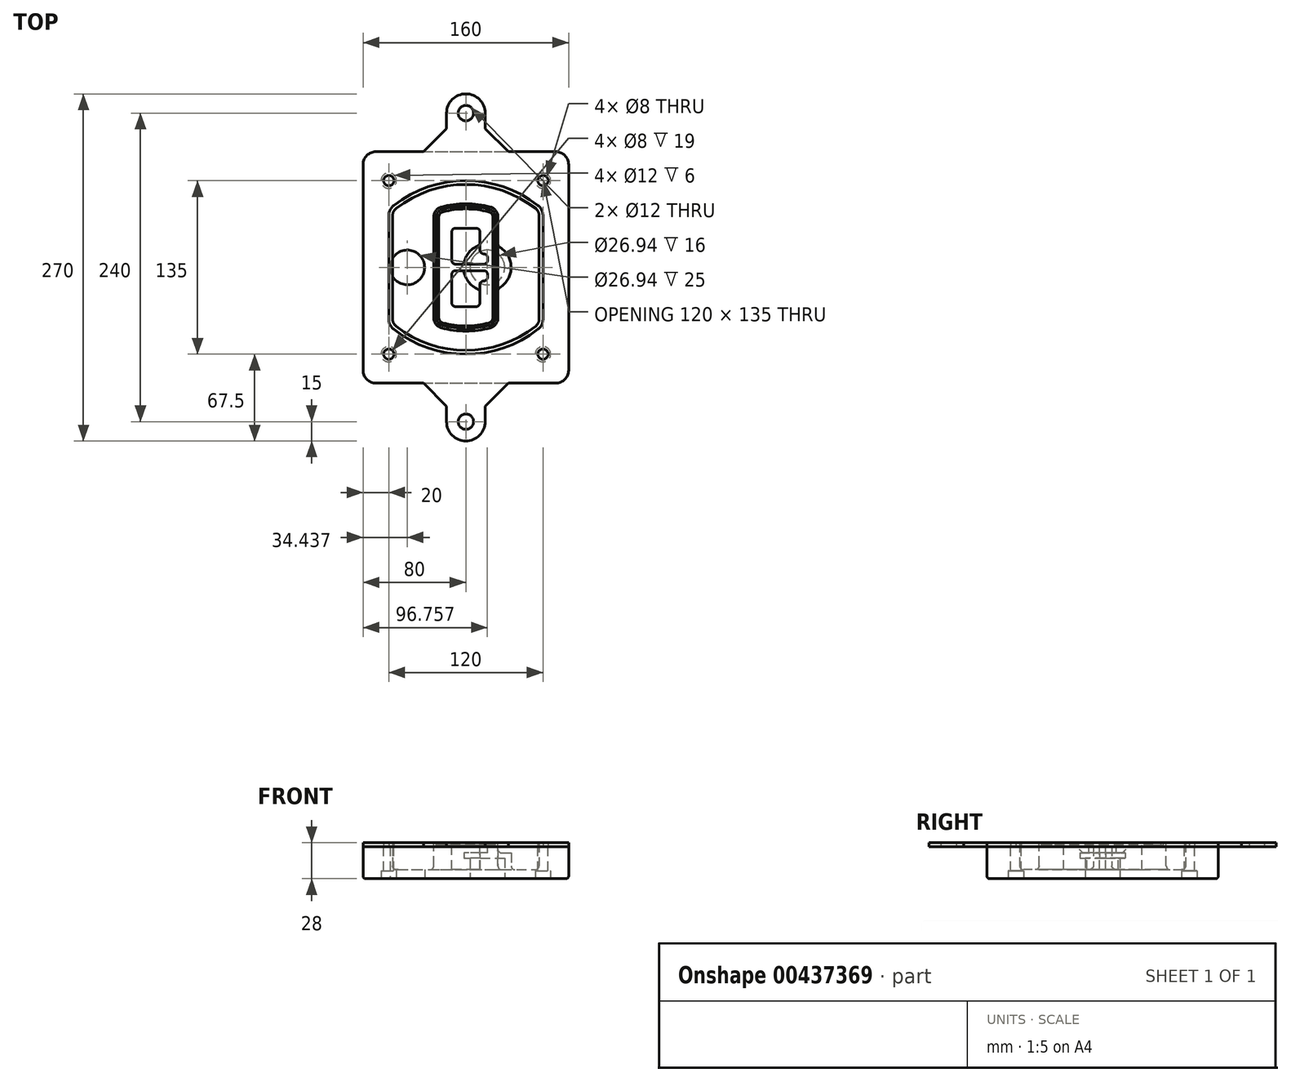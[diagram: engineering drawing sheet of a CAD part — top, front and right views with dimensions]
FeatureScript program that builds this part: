
annotation { "Feature Type Name" : "Feature", "Feature Type Description" : "" }
export const myFeature = defineFeature(function(context is Context, id is Id, definition is map)
    precondition{}
    {
        {
            var Q0;
            Q0=qCreatedBy(makeId("Top.planeOp"),FACE);
            var sketch = newSketch(context, id + "F0", { "sketchPlane" : qUnion([Q0])});
            skPoint(sketch, "E0.rect.middle", {"position": v(0, 0) * mm});
            skLineSegment(sketch, "E1.bottom", {"start": v(-70, -90) * mm, "end": v(70, -90) * mm});
            skLineSegment(sketch, "E1.top", {"start": v(-70, 90) * mm, "end": v(70, 90) * mm});
            skLineSegment(sketch, "E1.left", {"start": v(-80, -80) * mm, "end": v(-80, 80) * mm});
            skLineSegment(sketch, "E1.right", {"start": v(80, -80) * mm, "end": v(80, 80) * mm});
            skLineSegment(sketch, "E2", {"start": v(-80, 90) * mm, "end": v(80, -90) * mm, "construction": true});
            skLineSegment(sketch, "E3", {"start": v(80, 90) * mm, "end": v(-80, -90) * mm, "construction": true});
            skCircle(sketch, "E4", {"center": v(-60, 67.5) * mm, "radius": 4 * mm});
            skCircle(sketch, "E5", {"center": v(60, 67.5) * mm, "radius": 4 * mm});
            skCircle(sketch, "E6", {"center": v(60, -67.5) * mm, "radius": 4 * mm});
            skCircle(sketch, "E7", {"center": v(-60, -67.5) * mm, "radius": 4 * mm});
            skLineSegment(sketch, "E8", {"start": v(-60, 67.5) * mm, "end": v(60, 67.5) * mm, "construction": true});
            skLineSegment(sketch, "E9", {"start": v(60, 67.5) * mm, "end": v(60, -67.5) * mm, "construction": true});
            skLineSegment(sketch, "E10", {"start": v(60, -67.5) * mm, "end": v(-60, -67.5) * mm, "construction": true});
            skLineSegment(sketch, "E11", {"start": v(-60, -67.5) * mm, "end": v(-60, 67.5) * mm, "construction": true});
            skLineSegment(sketch, "E12", {"start": v(-60, 40.3) * mm, "end": v(-60, -40.3) * mm});
            skLineSegment(sketch, "E13", {"start": v(60, 40.3) * mm, "end": v(60, -40.3) * mm});
            skArc(sketch, "E14", {"start": v(56.15, 48.18) * mm, "mid": v(0, 67.5) * mm, "end": v(-56.15, 48.18) * mm});
            skArc(sketch, "E15", {"start": v(-56.15, -48.18) * mm, "mid": v(0, -67.5) * mm, "end": v(56.15, -48.18) * mm});
            skLineSegment(sketch, "E16", {"start": v(-60, 0) * mm, "end": v(60, 0) * mm, "construction": true});
            skPoint(sketch, "E17.visualSharp", {"position": v(-60, -45) * mm});
            skArc(sketch, "E17.filletArc", {"start": v(-60, -40.3) * mm, "mid": v(-58.99, -44.68) * mm, "end": v(-56.15, -48.18) * mm});
            skPoint(sketch, "E18.visualSharp", {"position": v(-60, 45) * mm});
            skArc(sketch, "E18.filletArc", {"start": v(-56.15, 48.18) * mm, "mid": v(-58.99, 44.68) * mm, "end": v(-60, 40.3) * mm});
            skPoint(sketch, "E19.visualSharp", {"position": v(60, 45) * mm});
            skArc(sketch, "E19.filletArc", {"start": v(60, 40.3) * mm, "mid": v(58.99, 44.68) * mm, "end": v(56.15, 48.18) * mm});
            skPoint(sketch, "E20.visualSharp", {"position": v(60, -45) * mm});
            skArc(sketch, "E20.filletArc", {"start": v(56.15, -48.18) * mm, "mid": v(58.99, -44.68) * mm, "end": v(60, -40.3) * mm});
            skPoint(sketch, "E21.visualSharp", {"position": v(-80, 90) * mm});
            skArc(sketch, "E21.filletArc", {"start": v(-70, 90) * mm, "mid": v(-77.07, 87.07) * mm, "end": v(-80, 80) * mm});
            skPoint(sketch, "E22.visualSharp", {"position": v(80, 90) * mm});
            skArc(sketch, "E22.filletArc", {"start": v(80, 80) * mm, "mid": v(77.07, 87.07) * mm, "end": v(70, 90) * mm});
            skPoint(sketch, "E23.visualSharp", {"position": v(80, -90) * mm});
            skArc(sketch, "E23.filletArc", {"start": v(70, -90) * mm, "mid": v(77.07, -87.07) * mm, "end": v(80, -80) * mm});
            skPoint(sketch, "E24.visualSharp", {"position": v(-80, -90) * mm});
            skArc(sketch, "E24.filletArc", {"start": v(-80, -80) * mm, "mid": v(-77.07, -87.07) * mm, "end": v(-70, -90) * mm});
            skArc(sketch, "E25.0", {"start": v(57, 40.3) * mm, "mid": v(56.3, 43.36) * mm, "end": v(54.3, 45.81) * mm});
            skLineSegment(sketch, "E25.1", {"start": v(57, 40.3) * mm, "end": v(57, -40.3) * mm});
            skArc(sketch, "E25.2", {"start": v(54.3, -45.81) * mm, "mid": v(56.3, -43.36) * mm, "end": v(57, -40.3) * mm});
            skArc(sketch, "E25.3", {"start": v(-54.3, -45.81) * mm, "mid": v(0, -64.5) * mm, "end": v(54.3, -45.81) * mm});
            skArc(sketch, "E25.4", {"start": v(-57, -40.3) * mm, "mid": v(-56.3, -43.36) * mm, "end": v(-54.3, -45.81) * mm});
            skArc(sketch, "E25.5", {"start": v(54.3, 45.81) * mm, "mid": v(0, 64.5) * mm, "end": v(-54.3, 45.81) * mm});
            skLineSegment(sketch, "E25.6", {"start": v(-57, 40.3) * mm, "end": v(-57, -40.3) * mm});
            skArc(sketch, "E25.7", {"start": v(-54.3, 45.81) * mm, "mid": v(-56.3, 43.36) * mm, "end": v(-57, 40.3) * mm});
            skArc(sketch, "E26.0", {"start": v(-58.62, 51.33) * mm, "mid": v(-62.58, 46.43) * mm, "end": v(-64, 40.3) * mm});
            skArc(sketch, "E26.1", {"start": v(58.62, 51.33) * mm, "mid": v(0, 71.5) * mm, "end": v(-58.62, 51.33) * mm});
            skArc(sketch, "E26.2", {"start": v(64, 40.3) * mm, "mid": v(62.58, 46.43) * mm, "end": v(58.62, 51.33) * mm});
            skLineSegment(sketch, "E26.3", {"start": v(64, 40.3) * mm, "end": v(64, -40.3) * mm});
            skArc(sketch, "E26.4", {"start": v(58.62, -51.33) * mm, "mid": v(62.58, -46.43) * mm, "end": v(64, -40.3) * mm});
            skLineSegment(sketch, "E26.5", {"start": v(-64, 40.3) * mm, "end": v(-64, -40.3) * mm});
            skArc(sketch, "E26.6", {"start": v(-58.62, -51.33) * mm, "mid": v(0, -71.5) * mm, "end": v(58.62, -51.33) * mm});
            skArc(sketch, "E26.7", {"start": v(-64, -40.3) * mm, "mid": v(-62.58, -46.43) * mm, "end": v(-58.62, -51.33) * mm});
            skSolve(sketch);
        }
        {
            var Q0;
            Q0=makeQuery(id+"F0.imprint","IMPRINT",FACE,{"disambiguationData":[TD([[makeQuery(id+"F0.imprint","IMPRINT",EDGE,{"derivedFrom":sQuery(id+"F0.wireOp",EDGE,"E1.bottom")}),1.0]])]});
            var Q1;
            Q1=makeQuery(id+"F0.imprint","IMPRINT",FACE,{"disambiguationData":[TD([[makeQuery(id+"F0.imprint","IMPRINT",EDGE,{"derivedFrom":sQuery(id+"F0.wireOp",EDGE,"E12")}),1.0]])]});
            var Q2;
            Q2=makeQuery(id+"F0.imprint","IMPRINT",FACE,{"disambiguationData":[TD([[makeQuery(id+"F0.imprint","IMPRINT",EDGE,{"derivedFrom":sQuery(id+"F0.wireOp",EDGE,"E25.0")}),1.0]])]});
            var Q3;
            Q3=makeQuery(id+"F0.imprint","IMPRINT",FACE,{"disambiguationData":[TD([[makeQuery(id+"F0.imprint","IMPRINT",EDGE,{"derivedFrom":sQuery(id+"F0.wireOp",EDGE,"E12")}),-1.0]])]});
            extrude(context, id + "F1", {"entities" : qUnion([Q0, Q1, Q2, Q3]), "oppositeDirection" : true, "depth" : 25 * mm});
        }
        {
            var Q0;
            Q0=makeQuery(id+"F0.imprint","IMPRINT",FACE,{"disambiguationData":[TD([[makeQuery(id+"F0.imprint","IMPRINT",EDGE,{"derivedFrom":sQuery(id+"F0.wireOp",EDGE,"E12")}),1.0]])]});
            extrude(context, id + "F2", {"entities" : qUnion([Q0]), "operationType" : NewBodyOperationType.ADD, "depth" : 3 * mm});
        }
        {
            var Q0;
            Q0=makeQuery(id+"F0.imprint","IMPRINT",FACE,{"disambiguationData":[TD([[makeQuery(id+"F0.imprint","IMPRINT",EDGE,{"derivedFrom":sQuery(id+"F0.wireOp",EDGE,"E25.0")}),1.0]])]});
            extrude(context, id + "F3", {"entities" : qUnion([Q0]), "operationType" : NewBodyOperationType.REMOVE, "oppositeDirection" : true, "depth" : 18 * mm});
        }
        {
            var Q0;
            Q0=makeQuery(id+"F2.opExtrude","CAP_FACE",FACE,{"disambiguationData":[OSD([sQuery(id+"F0.wireOp",EDGE,"E12"),sQuery(id+"F0.wireOp",EDGE,"E13"),sQuery(id+"F0.wireOp",EDGE,"E14"),sQuery(id+"F0.wireOp",EDGE,"E15"),sQuery(id+"F0.wireOp",EDGE,"E17.filletArc"),sQuery(id+"F0.wireOp",EDGE,"E18.filletArc"),sQuery(id+"F0.wireOp",EDGE,"E19.filletArc"),sQuery(id+"F0.wireOp",EDGE,"E20.filletArc"),sQuery(id+"F0.wireOp",EDGE,"E25.0"),sQuery(id+"F0.wireOp",EDGE,"E25.1"),sQuery(id+"F0.wireOp",EDGE,"E25.2"),sQuery(id+"F0.wireOp",EDGE,"E25.3"),sQuery(id+"F0.wireOp",EDGE,"E25.4"),sQuery(id+"F0.wireOp",EDGE,"E25.5"),sQuery(id+"F0.wireOp",EDGE,"E25.6"),sQuery(id+"F0.wireOp",EDGE,"E25.7")])],"isStart":false});
            var sketch = newSketch(context, id + "F4", { "sketchPlane" : qUnion([Q0])});
            skArc(sketch, "E27.0", {"start": v(-19.08, -46.97) * mm, "mid": v(0, -49.5) * mm, "end": v(19.08, -46.97) * mm});
            skArc(sketch, "E28.0", {"start": v(19.08, 46.97) * mm, "mid": v(0, 49.5) * mm, "end": v(-19.08, 46.97) * mm});
            skLineSegment(sketch, "E29", {"start": v(-25, 39.25) * mm, "end": v(-25, -39.25) * mm});
            skLineSegment(sketch, "E30", {"start": v(25, 39.25) * mm, "end": v(25, -39.25) * mm});
            skLineSegment(sketch, "E31", {"start": v(-25, 45.1) * mm, "end": v(25, 45.1) * mm, "construction": true});
            skLineSegment(sketch, "E32", {"start": v(-25, -45.1) * mm, "end": v(25, -45.1) * mm, "construction": true});
            skPoint(sketch, "E33.visualSharp", {"position": v(-25, 45.1) * mm});
            skArc(sketch, "E33.filletArc", {"start": v(-19.08, 46.97) * mm, "mid": v(-23.35, 44.11) * mm, "end": v(-25, 39.25) * mm});
            skPoint(sketch, "E34.visualSharp", {"position": v(25, 45.1) * mm});
            skArc(sketch, "E34.filletArc", {"start": v(25, 39.25) * mm, "mid": v(23.35, 44.11) * mm, "end": v(19.08, 46.97) * mm});
            skPoint(sketch, "E35.visualSharp", {"position": v(25, -45.1) * mm});
            skArc(sketch, "E35.filletArc", {"start": v(19.08, -46.97) * mm, "mid": v(23.35, -44.11) * mm, "end": v(25, -39.25) * mm});
            skPoint(sketch, "E36.visualSharp", {"position": v(-25, -45.1) * mm});
            skArc(sketch, "E36.filletArc", {"start": v(-25, -39.25) * mm, "mid": v(-23.35, -44.11) * mm, "end": v(-19.08, -46.97) * mm});
            skArc(sketch, "E37.0", {"start": v(54.3, 45.81) * mm, "mid": v(0, 64.5) * mm, "end": v(-54.3, 45.81) * mm});
            skArc(sketch, "E37.1", {"start": v(-54.3, 45.81) * mm, "mid": v(-56.3, 43.36) * mm, "end": v(-57, 40.3) * mm});
            skLineSegment(sketch, "E37.2", {"start": v(-57, 40.3) * mm, "end": v(-57, -40.3) * mm});
            skArc(sketch, "E37.3", {"start": v(-57, -40.3) * mm, "mid": v(-56.3, -43.36) * mm, "end": v(-54.3, -45.81) * mm});
            skArc(sketch, "E37.4", {"start": v(-54.3, -45.81) * mm, "mid": v(0, -64.5) * mm, "end": v(54.3, -45.81) * mm});
            skArc(sketch, "E37.5", {"start": v(54.3, -45.81) * mm, "mid": v(56.3, -43.36) * mm, "end": v(57, -40.3) * mm});
            skLineSegment(sketch, "E37.6", {"start": v(57, 40.3) * mm, "end": v(57, -40.3) * mm});
            skArc(sketch, "E37.7", {"start": v(57, 40.3) * mm, "mid": v(56.3, 43.36) * mm, "end": v(54.3, 45.81) * mm});
            skLineSegment(sketch, "E38.0", {"start": v(23, 39.25) * mm, "end": v(23, -39.25) * mm});
            skArc(sketch, "E38.1", {"start": v(18.56, -45.04) * mm, "mid": v(21.76, -42.9) * mm, "end": v(23, -39.25) * mm});
            skArc(sketch, "E38.2", {"start": v(-18.56, -45.04) * mm, "mid": v(0, -47.5) * mm, "end": v(18.56, -45.04) * mm});
            skArc(sketch, "E38.3", {"start": v(-23, -39.25) * mm, "mid": v(-21.76, -42.9) * mm, "end": v(-18.56, -45.04) * mm});
            skLineSegment(sketch, "E38.4", {"start": v(-23, 39.25) * mm, "end": v(-23, -39.25) * mm});
            skArc(sketch, "E38.5", {"start": v(23, 39.25) * mm, "mid": v(21.76, 42.9) * mm, "end": v(18.56, 45.04) * mm});
            skArc(sketch, "E38.6", {"start": v(-18.56, 45.04) * mm, "mid": v(-21.76, 42.9) * mm, "end": v(-23, 39.25) * mm});
            skArc(sketch, "E38.7", {"start": v(18.56, 45.04) * mm, "mid": v(0, 47.5) * mm, "end": v(-18.56, 45.04) * mm});
            skArc(sketch, "E39.0", {"start": v(21, 39.25) * mm, "mid": v(20.18, 41.68) * mm, "end": v(18.04, 43.1) * mm});
            skLineSegment(sketch, "E39.1", {"start": v(21, 39.25) * mm, "end": v(21, -39.25) * mm});
            skArc(sketch, "E39.2", {"start": v(18.04, -43.1) * mm, "mid": v(20.18, -41.68) * mm, "end": v(21, -39.25) * mm});
            skArc(sketch, "E39.3", {"start": v(-18.04, -43.1) * mm, "mid": v(0, -45.5) * mm, "end": v(18.04, -43.1) * mm});
            skArc(sketch, "E39.4", {"start": v(-21, -39.25) * mm, "mid": v(-20.18, -41.68) * mm, "end": v(-18.04, -43.1) * mm});
            skArc(sketch, "E39.5", {"start": v(18.04, 43.1) * mm, "mid": v(0, 45.5) * mm, "end": v(-18.04, 43.1) * mm});
            skLineSegment(sketch, "E39.6", {"start": v(-21, 39.25) * mm, "end": v(-21, -39.25) * mm});
            skArc(sketch, "E39.7", {"start": v(-18.04, 43.1) * mm, "mid": v(-20.18, 41.68) * mm, "end": v(-21, 39.25) * mm});
            skLineSegment(sketch, "E40", {"start": v(-25, 0) * mm, "end": v(25, 0) * mm, "construction": true});
            skLineSegment(sketch, "E41", {"start": v(-11, 5.5) * mm, "end": v(-11, 27.5) * mm});
            skLineSegment(sketch, "E42", {"start": v(-8, 30.5) * mm, "end": v(8, 30.5) * mm});
            skLineSegment(sketch, "E43", {"start": v(11, 27.5) * mm, "end": v(11, 13.5) * mm});
            skLineSegment(sketch, "E44", {"start": v(14, 10.5) * mm, "end": v(14, 10.5) * mm});
            skLineSegment(sketch, "E45", {"start": v(17, 7.5) * mm, "end": v(17, 5.5) * mm});
            skLineSegment(sketch, "E46", {"start": v(14, 2.5) * mm, "end": v(-8, 2.5) * mm});
            skPoint(sketch, "E47.visualSharp", {"position": v(-11, 30.5) * mm});
            skArc(sketch, "E47.filletArc", {"start": v(-8, 30.5) * mm, "mid": v(-10.12, 29.62) * mm, "end": v(-11, 27.5) * mm});
            skPoint(sketch, "E48.visualSharp", {"position": v(11, 30.5) * mm});
            skArc(sketch, "E48.filletArc", {"start": v(11, 27.5) * mm, "mid": v(10.12, 29.62) * mm, "end": v(8, 30.5) * mm});
            skPoint(sketch, "E49.visualSharp", {"position": v(11, 10.5) * mm});
            skArc(sketch, "E49.filletArc", {"start": v(11, 13.5) * mm, "mid": v(11.88, 11.38) * mm, "end": v(14, 10.5) * mm});
            skPoint(sketch, "E50.visualSharp", {"position": v(17, 10.5) * mm});
            skArc(sketch, "E50.filletArc", {"start": v(17, 7.5) * mm, "mid": v(16.12, 9.62) * mm, "end": v(14, 10.5) * mm});
            skPoint(sketch, "E51.visualSharp", {"position": v(17, 2.5) * mm});
            skArc(sketch, "E51.filletArc", {"start": v(14, 2.5) * mm, "mid": v(16.12, 3.38) * mm, "end": v(17, 5.5) * mm});
            skPoint(sketch, "E52.visualSharp", {"position": v(-11, 2.5) * mm});
            skArc(sketch, "E52.filletArc", {"start": v(-11, 5.5) * mm, "mid": v(-10.12, 3.38) * mm, "end": v(-8, 2.5) * mm});
            skLineSegment(sketch, "E53.0.MirrorCS", {"start": v(14, -2.5) * mm, "end": v(-8, -2.5) * mm});
            skArc(sketch, "E54.0.MirrorCS", {"start": v(-11, -5.5) * mm, "mid": v(-10.12, -3.38) * mm, "end": v(-8, -2.5) * mm});
            skLineSegment(sketch, "E55.0.MirrorCS", {"start": v(-11, -5.5) * mm, "end": v(-11, -27.5) * mm});
            skArc(sketch, "E56.0.MirrorCS", {"start": v(-8, -30.5) * mm, "mid": v(-10.12, -29.62) * mm, "end": v(-11, -27.5) * mm});
            skLineSegment(sketch, "E57.0.MirrorCS", {"start": v(-8, -30.5) * mm, "end": v(8, -30.5) * mm});
            skArc(sketch, "E58.0.MirrorCS", {"start": v(11, -27.5) * mm, "mid": v(10.12, -29.62) * mm, "end": v(8, -30.5) * mm});
            skLineSegment(sketch, "E59.0.MirrorCS", {"start": v(11, -27.5) * mm, "end": v(11, -13.5) * mm});
            skArc(sketch, "E60.0.MirrorCS", {"start": v(11, -13.5) * mm, "mid": v(11.88, -11.38) * mm, "end": v(14, -10.5) * mm});
            skArc(sketch, "E61.0.MirrorCS", {"start": v(17, -7.5) * mm, "mid": v(16.12, -9.62) * mm, "end": v(14, -10.5) * mm});
            skLineSegment(sketch, "E62.0.MirrorCS", {"start": v(17, -7.5) * mm, "end": v(17, -5.5) * mm});
            skArc(sketch, "E63.0.MirrorCS", {"start": v(14, -2.5) * mm, "mid": v(16.12, -3.38) * mm, "end": v(17, -5.5) * mm});
            skSolve(sketch);
        }
        {
            var Q0;
            Q0=makeQuery(id+"F4.imprint","IMPRINT",FACE,{"disambiguationData":[TD([[makeQuery(id+"F4.imprint","IMPRINT",EDGE,{"derivedFrom":sQuery(id+"F4.wireOp",EDGE,"E27.0")}),1.0]])]});
            var Q1;
            Q1=makeQuery(id+"F4.imprint","IMPRINT",FACE,{"disambiguationData":[TD([[makeQuery(id+"F4.imprint","IMPRINT",EDGE,{"derivedFrom":sQuery(id+"F4.wireOp",EDGE,"E38.0")}),-1.0]])]});
            var Q2;
            Q2=makeQuery(id+"F4.imprint","IMPRINT",FACE,{"disambiguationData":[TD([[makeQuery(id+"F4.imprint","IMPRINT",EDGE,{"derivedFrom":sQuery(id+"F4.wireOp",EDGE,"E39.0")}),1.0]])]});
            extrude(context, id + "F5", {"entities" : qUnion([Q0, Q1, Q2]), "operationType" : NewBodyOperationType.ADD, "endBound" : BoundingType.UP_TO_NEXT, "oppositeDirection" : true, "depth" : 25 * mm});
        }
        {
            var Q0;
            Q0=makeQuery(id+"F4.imprint","IMPRINT",FACE,{"disambiguationData":[TD([[makeQuery(id+"F4.imprint","IMPRINT",EDGE,{"derivedFrom":sQuery(id+"F4.wireOp",EDGE,"E38.0")}),-1.0]])]});
            extrude(context, id + "F6", {"entities" : qUnion([Q0]), "operationType" : NewBodyOperationType.REMOVE, "oppositeDirection" : true, "depth" : 2 * mm});
        }
        {
            var Q0;
            Q0=makeQuery(id+"F1.opExtrude","CAP_FACE",FACE,{"disambiguationData":[OSD([sQuery(id+"F0.wireOp",EDGE,"E1.bottom"),sQuery(id+"F0.wireOp",EDGE,"E1.top"),sQuery(id+"F0.wireOp",EDGE,"E1.left"),sQuery(id+"F0.wireOp",EDGE,"E1.right"),sQuery(id+"F0.wireOp",EDGE,"E4"),sQuery(id+"F0.wireOp",EDGE,"E5"),sQuery(id+"F0.wireOp",EDGE,"E6"),sQuery(id+"F0.wireOp",EDGE,"E7"),sQuery(id+"F0.wireOp",EDGE,"E21.filletArc"),sQuery(id+"F0.wireOp",EDGE,"E22.filletArc"),sQuery(id+"F0.wireOp",EDGE,"E23.filletArc"),sQuery(id+"F0.wireOp",EDGE,"E24.filletArc")])],"isStart":false});
            var sketch = newSketch(context, id + "F7", { "sketchPlane" : qUnion([Q0])});
            skCircle(sketch, "E64", {"center": v(16.76, 0) * mm, "radius": 13.47 * mm});
            skCircle(sketch, "E65", {"center": v(-45.56, 0) * mm, "radius": 13.47 * mm});
            skLineSegment(sketch, "E66", {"start": v(80, 0) * mm, "end": v(-80, 0) * mm});
            skCircle(sketch, "E67", {"center": v(16.76, 0) * mm, "radius": 18.47 * mm});
            skCircle(sketch, "E68", {"center": v(60, -67.5) * mm, "radius": 6 * mm});
            skCircle(sketch, "E69", {"center": v(-60, -67.5) * mm, "radius": 6 * mm});
            skCircle(sketch, "E70", {"center": v(-60, 67.5) * mm, "radius": 6 * mm});
            skCircle(sketch, "E71", {"center": v(60, 67.5) * mm, "radius": 6 * mm});
            skSolve(sketch);
        }
        {
            var Q0;
            {var subQ1=sQuery(id+"F7.wireOp",EDGE,"E66");var subQ4=sQuery(id+"F7.wireOp",EDGE,"E64");var subQ6=makeQuery(id+"F7.imprint","INTERSECT",VERTEX,{"disambiguationData":[OD(0.0)],"derivedFrom":[subQ4,subQ1]});Q0=makeQuery(id+"F7.imprint","IMPRINT",FACE,{"disambiguationData":[TD([[makeQuery(id+"F7.imprint","IMPRINT",EDGE,{"disambiguationData":[TD([[subQ6,-1.0]])],"derivedFrom":subQ4}),-1.0]])]});}
            var Q1;
            {var subQ0=sQuery(id+"F7.wireOp",EDGE,"E66");var subQ1=sQuery(id+"F7.wireOp",EDGE,"E64");var subQ3=makeQuery(id+"F7.imprint","INTERSECT",VERTEX,{"disambiguationData":[OD(0.0)],"derivedFrom":[subQ1,subQ0]});Q1=makeQuery(id+"F7.imprint","IMPRINT",FACE,{"disambiguationData":[TD([[makeQuery(id+"F7.imprint","IMPRINT",EDGE,{"disambiguationData":[TD([[subQ3,-1.0]])],"derivedFrom":subQ1}),1.0]])]});}
            var Q2;
            {var subQ0=sQuery(id+"F7.wireOp",EDGE,"E66");var subQ1=sQuery(id+"F7.wireOp",EDGE,"E64");var subQ3=makeQuery(id+"F7.imprint","INTERSECT",VERTEX,{"disambiguationData":[OD(0.0)],"derivedFrom":[subQ1,subQ0]});Q2=makeQuery(id+"F7.imprint","IMPRINT",FACE,{"disambiguationData":[TD([[makeQuery(id+"F7.imprint","IMPRINT",EDGE,{"disambiguationData":[TD([[subQ3,1.0]])],"derivedFrom":subQ1}),1.0]])]});}
            var Q3;
            {var subQ1=sQuery(id+"F7.wireOp",EDGE,"E66");var subQ4=sQuery(id+"F7.wireOp",EDGE,"E64");var subQ6=makeQuery(id+"F7.imprint","INTERSECT",VERTEX,{"disambiguationData":[OD(0.0)],"derivedFrom":[subQ4,subQ1]});Q3=makeQuery(id+"F7.imprint","IMPRINT",FACE,{"disambiguationData":[TD([[makeQuery(id+"F7.imprint","IMPRINT",EDGE,{"disambiguationData":[TD([[subQ6,1.0]])],"derivedFrom":subQ4}),-1.0]])]});}
            extrude(context, id + "F8", {"entities" : qUnion([Q0, Q1, Q2, Q3]), "operationType" : NewBodyOperationType.ADD, "oppositeDirection" : true, "depth" : 20 * mm});
        }
        {
            var Q0;
            {var subQ0=sQuery(id+"F7.wireOp",EDGE,"E66");var subQ1=sQuery(id+"F7.wireOp",EDGE,"E64");var subQ3=makeQuery(id+"F7.imprint","INTERSECT",VERTEX,{"disambiguationData":[OD(0.0)],"derivedFrom":[subQ1,subQ0]});Q0=makeQuery(id+"F7.imprint","IMPRINT",FACE,{"disambiguationData":[TD([[makeQuery(id+"F7.imprint","IMPRINT",EDGE,{"disambiguationData":[TD([[subQ3,-1.0]])],"derivedFrom":subQ1}),1.0]])]});}
            var Q1;
            {var subQ0=sQuery(id+"F7.wireOp",EDGE,"E66");var subQ1=sQuery(id+"F7.wireOp",EDGE,"E64");var subQ3=makeQuery(id+"F7.imprint","INTERSECT",VERTEX,{"disambiguationData":[OD(0.0)],"derivedFrom":[subQ1,subQ0]});Q1=makeQuery(id+"F7.imprint","IMPRINT",FACE,{"disambiguationData":[TD([[makeQuery(id+"F7.imprint","IMPRINT",EDGE,{"disambiguationData":[TD([[subQ3,1.0]])],"derivedFrom":subQ1}),1.0]])]});}
            extrude(context, id + "F9", {"entities" : qUnion([Q0, Q1]), "operationType" : NewBodyOperationType.REMOVE, "oppositeDirection" : true, "depth" : 16 * mm});
        }
        {
            var Q0;
            {var subQ0=sQuery(id+"F7.wireOp",EDGE,"E66");var subQ1=sQuery(id+"F7.wireOp",EDGE,"E65");var subQ3=makeQuery(id+"F7.imprint","INTERSECT",VERTEX,{"disambiguationData":[OD(0.0)],"derivedFrom":[subQ1,subQ0]});Q0=makeQuery(id+"F7.imprint","IMPRINT",FACE,{"disambiguationData":[TD([[makeQuery(id+"F7.imprint","IMPRINT",EDGE,{"disambiguationData":[TD([[subQ3,-1.0]])],"derivedFrom":subQ1}),1.0]])]});}
            var Q1;
            {var subQ0=sQuery(id+"F7.wireOp",EDGE,"E66");var subQ1=sQuery(id+"F7.wireOp",EDGE,"E65");var subQ3=makeQuery(id+"F7.imprint","INTERSECT",VERTEX,{"disambiguationData":[OD(0.0)],"derivedFrom":[subQ1,subQ0]});Q1=makeQuery(id+"F7.imprint","IMPRINT",FACE,{"disambiguationData":[TD([[makeQuery(id+"F7.imprint","IMPRINT",EDGE,{"disambiguationData":[TD([[subQ3,1.0]])],"derivedFrom":subQ1}),1.0]])]});}
            extrude(context, id + "F10", {"entities" : qUnion([Q0, Q1]), "operationType" : NewBodyOperationType.REMOVE, "oppositeDirection" : true, "depth" : 25 * mm});
        }
        {
            var Q0;
            Q0=makeQuery(id+"F7.imprint","IMPRINT",FACE,{"disambiguationData":[TD([[makeQuery(id+"F7.imprint","IMPRINT",EDGE,{"derivedFrom":sQuery(id+"F7.wireOp",EDGE,"E68")}),1.0]])]});
            var Q1;
            Q1=makeQuery(id+"F7.imprint","IMPRINT",FACE,{"disambiguationData":[TD([[makeQuery(id+"F7.imprint","IMPRINT",EDGE,{"derivedFrom":makeQuery(id+"F1.opExtrude","CAP_EDGE",EDGE,{"disambiguationData":[OSD([sQuery(id+"F0.wireOp",EDGE,"E5")])],"isStart":false})}),-1.0]])]});
            var Q2;
            Q2=makeQuery(id+"F7.imprint","IMPRINT",FACE,{"disambiguationData":[TD([[makeQuery(id+"F7.imprint","IMPRINT",EDGE,{"derivedFrom":sQuery(id+"F7.wireOp",EDGE,"E69")}),1.0]])]});
            var Q3;
            Q3=makeQuery(id+"F7.imprint","IMPRINT",FACE,{"disambiguationData":[TD([[makeQuery(id+"F7.imprint","IMPRINT",EDGE,{"derivedFrom":makeQuery(id+"F1.opExtrude","CAP_EDGE",EDGE,{"disambiguationData":[OSD([sQuery(id+"F0.wireOp",EDGE,"E4")])],"isStart":false})}),-1.0]])]});
            var Q4;
            Q4=makeQuery(id+"F7.imprint","IMPRINT",FACE,{"disambiguationData":[TD([[makeQuery(id+"F7.imprint","IMPRINT",EDGE,{"derivedFrom":sQuery(id+"F7.wireOp",EDGE,"E70")}),1.0]])]});
            var Q5;
            Q5=makeQuery(id+"F7.imprint","IMPRINT",FACE,{"disambiguationData":[TD([[makeQuery(id+"F7.imprint","IMPRINT",EDGE,{"derivedFrom":makeQuery(id+"F1.opExtrude","CAP_EDGE",EDGE,{"disambiguationData":[OSD([sQuery(id+"F0.wireOp",EDGE,"E7")])],"isStart":false})}),-1.0]])]});
            var Q6;
            Q6=makeQuery(id+"F7.imprint","IMPRINT",FACE,{"disambiguationData":[TD([[makeQuery(id+"F7.imprint","IMPRINT",EDGE,{"derivedFrom":sQuery(id+"F7.wireOp",EDGE,"E71")}),1.0]])]});
            var Q7;
            Q7=makeQuery(id+"F7.imprint","IMPRINT",FACE,{"disambiguationData":[TD([[makeQuery(id+"F7.imprint","IMPRINT",EDGE,{"derivedFrom":makeQuery(id+"F1.opExtrude","CAP_EDGE",EDGE,{"disambiguationData":[OSD([sQuery(id+"F0.wireOp",EDGE,"E6")])],"isStart":false})}),-1.0]])]});
            extrude(context, id + "F11", {"entities" : qUnion([Q0, Q1, Q2, Q3, Q4, Q5, Q6, Q7]), "operationType" : NewBodyOperationType.REMOVE, "oppositeDirection" : true, "depth" : 6 * mm});
        }
        {
            var Q0;
            Q0=makeQuery(id+"F9.boolean.opBoolean","COPY",FACE,{"derivedFrom":makeQuery(id+"F9.opExtrude","CAP_FACE",FACE,{"disambiguationData":[OSD([sQuery(id+"F7.wireOp",EDGE,"E64")])],"isStart":false})});
            var sketch = newSketch(context, id + "F12", { "sketchPlane" : qUnion([Q0])});
            skArc(sketch, "E72.0", {"start": v(11, 17.55) * mm, "mid": v(2.57, 11.82) * mm, "end": v(-1.54, 2.5) * mm});
            skArc(sketch, "E72.1", {"start": v(-1.54, -2.5) * mm, "mid": v(2.57, -11.82) * mm, "end": v(11, -17.55) * mm});
            skLineSegment(sketch, "E73", {"start": v(-1.54, -2.5) * mm, "end": v(14, -2.5) * mm});
            skLineSegment(sketch, "E74.0", {"start": v(14, 2.5) * mm, "end": v(-1.54, 2.5) * mm});
            skArc(sketch, "E74.1", {"start": v(14, 2.5) * mm, "mid": v(16.12, 3.38) * mm, "end": v(17, 5.5) * mm});
            skLineSegment(sketch, "E74.2", {"start": v(17, 7.5) * mm, "end": v(17, 5.5) * mm});
            skArc(sketch, "E74.3", {"start": v(17, 7.5) * mm, "mid": v(16.12, 9.62) * mm, "end": v(14, 10.5) * mm});
            skArc(sketch, "E74.4", {"start": v(11, 13.5) * mm, "mid": v(11.88, 11.38) * mm, "end": v(14, 10.5) * mm});
            skLineSegment(sketch, "E74.5", {"start": v(11, 17.55) * mm, "end": v(11, 13.5) * mm});
            skLineSegment(sketch, "E74.7", {"start": v(14, -2.5) * mm, "end": v(-1.54, -2.5) * mm});
            skArc(sketch, "E74.8", {"start": v(14, -2.5) * mm, "mid": v(16.12, -3.38) * mm, "end": v(17, -5.5) * mm});
            skLineSegment(sketch, "E74.9", {"start": v(17, -7.5) * mm, "end": v(17, -5.5) * mm});
            skArc(sketch, "E74.10", {"start": v(17, -7.5) * mm, "mid": v(16.12, -9.62) * mm, "end": v(14, -10.5) * mm});
            skArc(sketch, "E74.11", {"start": v(11, -13.5) * mm, "mid": v(11.88, -11.38) * mm, "end": v(14, -10.5) * mm});
            skLineSegment(sketch, "E74.12", {"start": v(11, -17.55) * mm, "end": v(11, -13.5) * mm});
            skPoint(sketch, "E75.orphan", {"position": v(11, -27.5) * mm});
            skPoint(sketch, "E76.orphan", {"position": v(-8, -2.5) * mm});
            skPoint(sketch, "E77.orphan", {"position": v(-8, 2.5) * mm});
            skPoint(sketch, "E78.orphan", {"position": v(11, 27.5) * mm});
            skSolve(sketch);
        }
        {
            var Q0;
            {var subQ7=sQuery(id+"F12.wireOp",EDGE,"E72.0");var subQ14=sQuery(id+"F12.wireOp",EDGE,"E72.1");var subQ16=sQuery(id+"F12.wireOp",EDGE,"E74.1");var subQ18=sQuery(id+"F12.wireOp",EDGE,"E74.8");Q0=qUnion([makeQuery(id+"F12.imprint","IMPRINT",FACE,{"disambiguationData":[TD([[makeQuery(id+"F12.imprint","IMPRINT",EDGE,{"derivedFrom":subQ7}),1.0]])]}),makeQuery(id+"F12.imprint","IMPRINT",FACE,{"disambiguationData":[TD([[makeQuery(id+"F12.imprint","IMPRINT",EDGE,{"derivedFrom":subQ14}),1.0]])]}),makeQuery(id+"F12.imprint","IMPRINT",FACE,{"disambiguationData":[TD([[makeQuery(id+"F12.imprint","IMPRINT",EDGE,{"derivedFrom":subQ16}),1.0]])]}),makeQuery(id+"F12.imprint","IMPRINT",FACE,{"disambiguationData":[TD([[makeQuery(id+"F12.imprint","IMPRINT",EDGE,{"derivedFrom":subQ18}),-1.0]])]})]);}
            var Q1;
            Q1=makeQuery(id+"F5.boolean.opBoolean","SPLIT",FACE,{"disambiguationData":[TD([makeQuery(id+"F5.opExtrude","SWEPT_FACE",FACE,{"disambiguationData":[OSD([sQuery(id+"F4.wireOp",EDGE,"E41")])]})])],"derivedFrom":makeQuery(id+"F3.boolean.opBoolean","COPY",FACE,{"derivedFrom":makeQuery(id+"F3.opExtrude","CAP_FACE",FACE,{"disambiguationData":[OSD([sQuery(id+"F0.wireOp",EDGE,"E25.0"),sQuery(id+"F0.wireOp",EDGE,"E25.1"),sQuery(id+"F0.wireOp",EDGE,"E25.2"),sQuery(id+"F0.wireOp",EDGE,"E25.3"),sQuery(id+"F0.wireOp",EDGE,"E25.4"),sQuery(id+"F0.wireOp",EDGE,"E25.5"),sQuery(id+"F0.wireOp",EDGE,"E25.6"),sQuery(id+"F0.wireOp",EDGE,"E25.7")])],"isStart":false})})});
            extrude(context, id + "F13", {"entities" : qUnion([Q0]), "operationType" : NewBodyOperationType.REMOVE, "endBound" : BoundingType.UP_TO_SURFACE, "endBoundEntityFace" : qUnion([Q1]), "depth" : 25 * mm});
        }
        {
            var Q0;
            Q0=makeQuery(id+"F3.boolean.opBoolean","COPY",EDGE,{"derivedFrom":makeQuery(id+"F3.opExtrude","CAP_EDGE",EDGE,{"disambiguationData":[OSD([sQuery(id+"F0.wireOp",EDGE,"E25.6")])],"isStart":false})});
            var Q1;
            Q1=makeQuery(id+"F8.boolean.opBoolean","INTERSECT",EDGE,{"derivedFrom":[makeQuery(id+"F5.opExtrude","SWEPT_FACE",FACE,{"disambiguationData":[OSD([sQuery(id+"F4.wireOp",EDGE,"E30")])]}),makeQuery(id+"F8.opExtrude","CAP_FACE",FACE,{"disambiguationData":[OSD([sQuery(id+"F7.wireOp",EDGE,"E67")])],"isStart":false})]});
            var Q2;
            Q2=makeQuery(id+"F8.boolean.opBoolean","INTERSECT",EDGE,{"disambiguationData":[OD(1.0)],"derivedFrom":[makeQuery(id+"F5.opExtrude","SWEPT_FACE",FACE,{"disambiguationData":[OSD([sQuery(id+"F4.wireOp",EDGE,"E30")])]}),makeQuery(id+"F8.opExtrude","SWEPT_FACE",FACE,{"disambiguationData":[OSD([sQuery(id+"F7.wireOp",EDGE,"E67")])]})]});
            var Q3;
            {var subQ0=sQuery(id+"F4.wireOp",EDGE,"E30");Q3=makeQuery(id+"F8.boolean.opBoolean","SPLIT",EDGE,{"disambiguationData":[TD([makeQuery(id+"F5.opExtrude","SWEPT_FACE",FACE,{"disambiguationData":[OSD([sQuery(id+"F4.wireOp",EDGE,"E35.filletArc")])]})])],"derivedFrom":makeQuery(id+"F5.opExtrude","CAP_EDGE",EDGE,{"disambiguationData":[OSD([subQ0])],"isStart":false})});}
            var Q4;
            {var subQ0=sQuery(id+"F0.wireOp",EDGE,"E25.7");var subQ1=sQuery(id+"F0.wireOp",EDGE,"E25.1");var subQ2=sQuery(id+"F0.wireOp",EDGE,"E25.6");var subQ3=sQuery(id+"F0.wireOp",EDGE,"E25.5");var subQ4=sQuery(id+"F0.wireOp",EDGE,"E25.4");var subQ5=sQuery(id+"F0.wireOp",EDGE,"E25.0");var subQ6=sQuery(id+"F0.wireOp",EDGE,"E25.2");var subQ7=sQuery(id+"F0.wireOp",EDGE,"E25.3");Q4=makeQuery(id+"F8.boolean.opBoolean","INTERSECT",EDGE,{"derivedFrom":[makeQuery(id+"F5.boolean.opBoolean","SPLIT",FACE,{"disambiguationData":[TD([makeQuery(id+"F2.opExtrude","SWEPT_FACE",FACE,{"disambiguationData":[OSD([subQ5])]})])],"derivedFrom":makeQuery(id+"F3.boolean.opBoolean","COPY",FACE,{"derivedFrom":makeQuery(id+"F3.opExtrude","CAP_FACE",FACE,{"disambiguationData":[OSD([subQ5,subQ1,subQ6,subQ7,subQ4,subQ3,subQ2,subQ0])],"isStart":false})})}),makeQuery(id+"F8.opExtrude","SWEPT_FACE",FACE,{"disambiguationData":[OSD([sQuery(id+"F7.wireOp",EDGE,"E67")])]})]});}
            var Q5;
            Q5=makeQuery(id+"F8.boolean.opBoolean","INTERSECT",EDGE,{"disambiguationData":[OD(0.0)],"derivedFrom":[makeQuery(id+"F5.opExtrude","SWEPT_FACE",FACE,{"disambiguationData":[OSD([sQuery(id+"F4.wireOp",EDGE,"E30")])]}),makeQuery(id+"F8.opExtrude","SWEPT_FACE",FACE,{"disambiguationData":[OSD([sQuery(id+"F7.wireOp",EDGE,"E67")])]})]});
            fillet(context, id + "F14", {"entities" : qUnion([Q0, Q1, Q2, Q3, Q4, Q5]), "radius" : 3 * mm, "tangentPropagation" : true, "allowEdgeOverflow" : false});
        }
        {
            var Q0;
            Q0=makeQuery(id+"F1.opExtrude","CAP_EDGE",EDGE,{"disambiguationData":[OSD([sQuery(id+"F0.wireOp",EDGE,"E1.bottom")])],"isStart":false});
            fillet(context, id + "F15", {"entities" : qUnion([Q0]), "radius" : 2 * mm, "tangentPropagation" : true, "allowEdgeOverflow" : false});
        }
        {
            var Q0;
            Q0=qCreatedBy(makeId("Top.planeOp"),FACE);
            var sketch = newSketch(context, id + "F16", { "sketchPlane" : qUnion([Q0])});
            skLineSegment(sketch, "E79.0", {"start": v(-80, -80) * mm, "end": v(-80, 80) * mm});
            skArc(sketch, "E79.1", {"start": v(-70, 90) * mm, "mid": v(-77.07, 87.07) * mm, "end": v(-80, 80) * mm});
            skCircle(sketch, "E79.2", {"center": v(-60, 67.5) * mm, "radius": 4 * mm});
            skLineSegment(sketch, "E79.3", {"start": v(-70, 90) * mm, "end": v(70, 90) * mm});
            skArc(sketch, "E79.4", {"start": v(80, 80) * mm, "mid": v(77.07, 87.07) * mm, "end": v(70, 90) * mm});
            skLineSegment(sketch, "E79.5", {"start": v(80, -80) * mm, "end": v(80, 80) * mm});
            skCircle(sketch, "E79.6", {"center": v(60, 67.5) * mm, "radius": 4 * mm});
            skArc(sketch, "E79.7", {"start": v(70, -90) * mm, "mid": v(77.07, -87.07) * mm, "end": v(80, -80) * mm});
            skLineSegment(sketch, "E79.8", {"start": v(-70, -90) * mm, "end": v(70, -90) * mm});
            skArc(sketch, "E79.9", {"start": v(-80, -80) * mm, "mid": v(-77.07, -87.07) * mm, "end": v(-70, -90) * mm});
            skCircle(sketch, "E79.10", {"center": v(-60, -67.5) * mm, "radius": 4 * mm});
            skCircle(sketch, "E79.11", {"center": v(60, -67.5) * mm, "radius": 4 * mm});
            skArc(sketch, "E79.12", {"start": v(56.15, -48.18) * mm, "mid": v(58.99, -44.68) * mm, "end": v(60, -40.3) * mm});
            skArc(sketch, "E79.13", {"start": v(-56.15, -48.18) * mm, "mid": v(0, -67.5) * mm, "end": v(56.15, -48.18) * mm});
            skLineSegment(sketch, "E79.14", {"start": v(60, 40.3) * mm, "end": v(60, -40.3) * mm});
            skArc(sketch, "E79.15", {"start": v(60, 40.3) * mm, "mid": v(58.99, 44.68) * mm, "end": v(56.15, 48.18) * mm});
            skArc(sketch, "E79.16", {"start": v(56.15, 48.18) * mm, "mid": v(0, 67.5) * mm, "end": v(-56.15, 48.18) * mm});
            skArc(sketch, "E79.17", {"start": v(-56.15, 48.18) * mm, "mid": v(-58.99, 44.68) * mm, "end": v(-60, 40.3) * mm});
            skLineSegment(sketch, "E79.18", {"start": v(-60, 40.3) * mm, "end": v(-60, -40.3) * mm});
            skArc(sketch, "E79.19", {"start": v(-60, -40.3) * mm, "mid": v(-58.99, -44.68) * mm, "end": v(-56.15, -48.18) * mm});
            skLineSegment(sketch, "E80", {"start": v(0, 90) * mm, "end": v(0, 120) * mm, "construction": true});
            skPoint(sketch, "E80.endSnap0", {"position": v(0, 90) * mm});
            skCircle(sketch, "E81", {"center": v(0, 120) * mm, "radius": 6 * mm});
            skArc(sketch, "E82", {"start": v(-15, 120) * mm, "mid": v(0, 135) * mm, "end": v(15, 120) * mm});
            skLineSegment(sketch, "E83", {"start": v(15, 120) * mm, "end": v(15, 108) * mm});
            skLineSegment(sketch, "E84", {"start": v(-15, 120) * mm, "end": v(-15, 108) * mm});
            skLineSegment(sketch, "E85", {"start": v(-15, 108) * mm, "end": v(-33, 90) * mm});
            skLineSegment(sketch, "E86", {"start": v(15, 108) * mm, "end": v(33, 90) * mm});
            skLineSegment(sketch, "E87", {"start": v(-80, 0) * mm, "end": v(80, 0) * mm, "construction": true});
            skLineSegment(sketch, "E88.MirrorCS", {"start": v(15, -108) * mm, "end": v(33, -90) * mm});
            skLineSegment(sketch, "E89.MirrorCS", {"start": v(-15, -108) * mm, "end": v(-33, -90) * mm});
            skCircle(sketch, "E90.MirrorC", {"center": v(0, -120) * mm, "radius": 6 * mm});
            skLineSegment(sketch, "E91.MirrorCS", {"start": v(15, -120) * mm, "end": v(15, -108) * mm});
            skArc(sketch, "E92.MirrorCS", {"start": v(-15, -120) * mm, "mid": v(0, -135) * mm, "end": v(15, -120) * mm});
            skLineSegment(sketch, "E93.MirrorCS", {"start": v(0, -90) * mm, "end": v(0, -120) * mm, "construction": true});
            skLineSegment(sketch, "E94.MirrorCS", {"start": v(-15, -120) * mm, "end": v(-15, -108) * mm});
            skSolve(sketch);
        }
        {
            var Q0;
            Q0 = qSketchRegion(id + "F16", true);
            var Q1;
            Q1=makeQuery(id+"F2.opExtrude","CAP_FACE",FACE,{"disambiguationData":[OSD([sQuery(id+"F0.wireOp",EDGE,"E12"),sQuery(id+"F0.wireOp",EDGE,"E13"),sQuery(id+"F0.wireOp",EDGE,"E14"),sQuery(id+"F0.wireOp",EDGE,"E15"),sQuery(id+"F0.wireOp",EDGE,"E17.filletArc"),sQuery(id+"F0.wireOp",EDGE,"E18.filletArc"),sQuery(id+"F0.wireOp",EDGE,"E19.filletArc"),sQuery(id+"F0.wireOp",EDGE,"E20.filletArc"),sQuery(id+"F0.wireOp",EDGE,"E25.0"),sQuery(id+"F0.wireOp",EDGE,"E25.1"),sQuery(id+"F0.wireOp",EDGE,"E25.2"),sQuery(id+"F0.wireOp",EDGE,"E25.3"),sQuery(id+"F0.wireOp",EDGE,"E25.4"),sQuery(id+"F0.wireOp",EDGE,"E25.5"),sQuery(id+"F0.wireOp",EDGE,"E25.6"),sQuery(id+"F0.wireOp",EDGE,"E25.7")])],"isStart":false});
            extrude(context, id + "F17", {"entities" : qUnion([Q0]), "endBound" : BoundingType.UP_TO_SURFACE, "endBoundEntityFace" : qUnion([Q1]), "depth" : 25 * mm});
        }
    });
